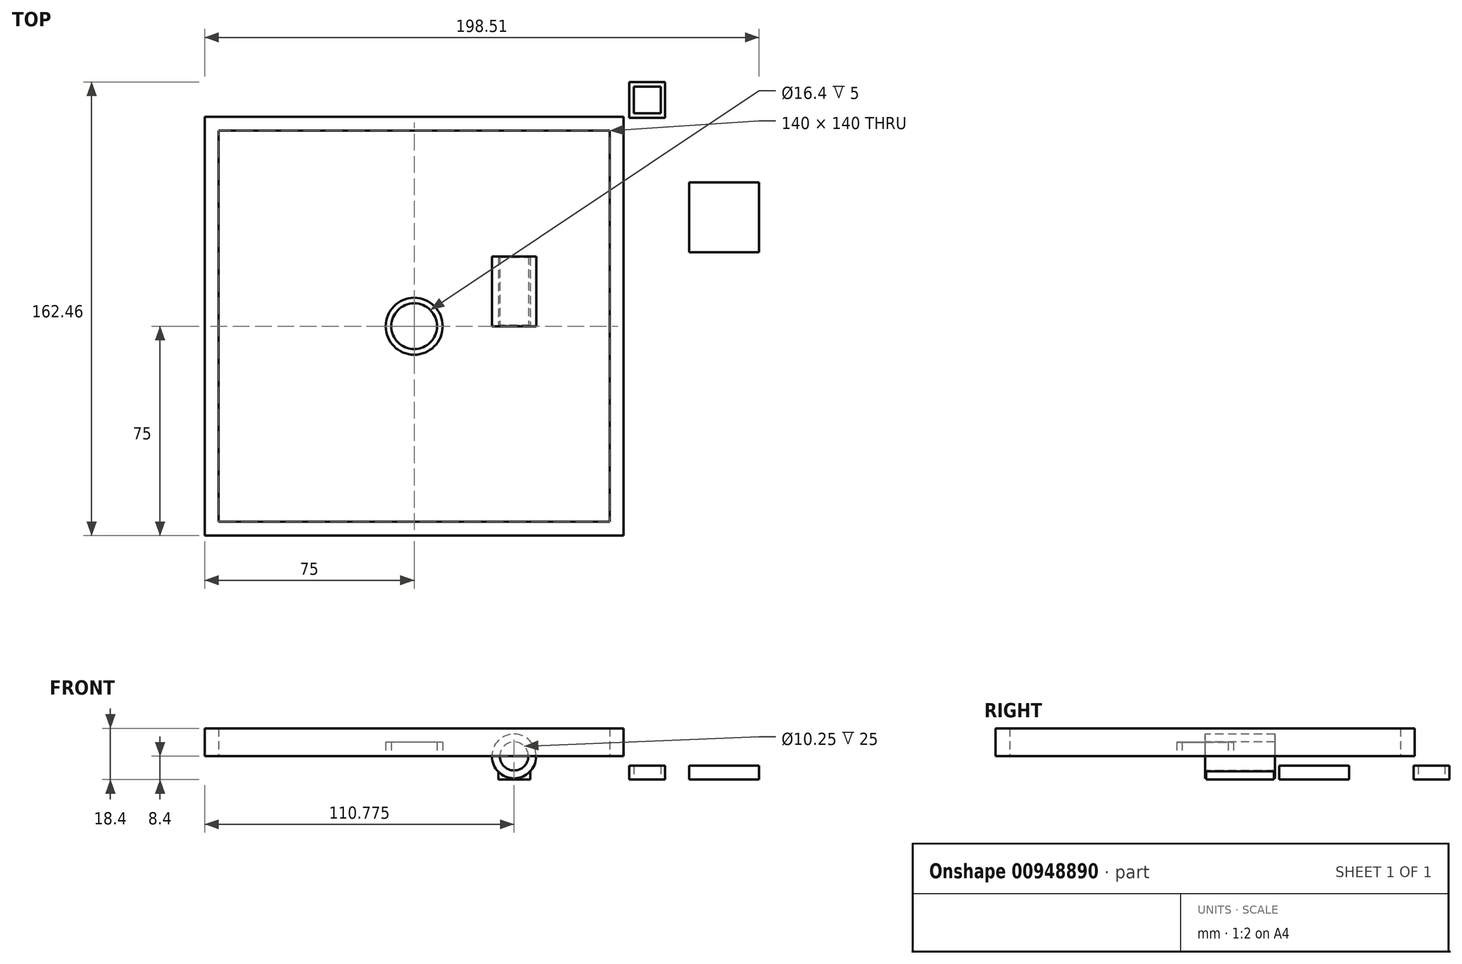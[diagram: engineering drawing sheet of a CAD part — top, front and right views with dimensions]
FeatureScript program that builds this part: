
annotation { "Feature Type Name" : "Feature", "Feature Type Description" : "" }
export const myFeature = defineFeature(function(context is Context, id is Id, definition is map)
    precondition{}
    {
        {
            var Q0;
            Q0=qCreatedBy(makeId("Top.planeOp"),FACE);
            var sketch = newSketch(context, id + "F0", { "sketchPlane" : qUnion([Q0])});
            skLineSegment(sketch, "E0.bottom", {"start": v(75, -75) * mm, "end": v(-75, -75) * mm});
            skLineSegment(sketch, "E0.top", {"start": v(75, 75) * mm, "end": v(-75, 75) * mm});
            skLineSegment(sketch, "E0.left", {"start": v(75, -75) * mm, "end": v(75, 75) * mm});
            skLineSegment(sketch, "E0.right", {"start": v(-75, -75) * mm, "end": v(-75, 75) * mm});
            skPoint(sketch, "E0.middle", {"position": v(0, 0) * mm});
            skLineSegment(sketch, "E1.bottom", {"start": v(70, -70) * mm, "end": v(-70, -70) * mm});
            skLineSegment(sketch, "E1.top", {"start": v(70, 70) * mm, "end": v(-70, 70) * mm});
            skLineSegment(sketch, "E1.left", {"start": v(70, -70) * mm, "end": v(70, 70) * mm});
            skLineSegment(sketch, "E1.right", {"start": v(-70, -70) * mm, "end": v(-70, 70) * mm});
            skCircle(sketch, "E2", {"center": v(0, 0) * mm, "radius": 8.2 * mm});
            skCircle(sketch, "E3", {"center": v(0, 0) * mm, "radius": 10.2 * mm});
            skCircle(sketch, "E4", {"center": v(35.77, 0) * mm, "radius": 5.12 * mm});
            skCircle(sketch, "E5", {"center": v(35.77, 0) * mm, "radius": 7.92 * mm});
            skLineSegment(sketch, "E6", {"start": v(0, 0) * mm, "end": v(-48.15, 0) * mm, "construction": true});
            skSolve(sketch);
        }
        {
            var Q0;
            Q0=makeQuery(id+"F0.imprint","IMPRINT",FACE,{"disambiguationData":[TD([[makeQuery(id+"F0.imprint","IMPRINT",EDGE,{"derivedFrom":sQuery(id+"F0.wireOp",EDGE,"E0.bottom")}),-1.0]])]});
            extrude(context, id + "F1", {"entities" : qUnion([Q0]), "depth" : 10 * mm, "offsetDistance" : 25 * mm});
        }
        {
            var Q0;
            Q0=makeQuery(id+"F0.imprint","IMPRINT",FACE,{"disambiguationData":[TD([[makeQuery(id+"F0.imprint","IMPRINT",EDGE,{"derivedFrom":sQuery(id+"F0.wireOp",EDGE,"E2")}),-1.0]])]});
            extrude(context, id + "F2", {"entities" : qUnion([Q0]), "depth" : 5 * mm, "offsetDistance" : 25 * mm});
        }
        {
            var Q0;
            Q0=makeQuery(id+"F0.imprint","IMPRINT",FACE,{"disambiguationData":[TD([[makeQuery(id+"F0.imprint","IMPRINT",EDGE,{"derivedFrom":sQuery(id+"F0.wireOp",EDGE,"E4")}),-1.0]])]});
            extrude(context, id + "F3", {"entities" : qUnion([Q0]), "depth" : 25 * mm, "offsetDistance" : 25 * mm});
        }
        {
            var Q0;
            Q0=makeQuery(id+"F3.opExtrude","SWEPT_BODY",BODY,{"disambiguationData":[OSD([sQuery(id+"F0.wireOp",EDGE,"E4"),sQuery(id+"F0.wireOp",EDGE,"E5")])]});
            var Q1;
            Q1=sQuery(id+"F0.wireOp",EDGE,"E6");
            var Q2;
            Q2=sQuery(id+"F0.wireOp",EDGE,"E6");
            transform(context, id + "F4", {"entities" : qUnion([Q0]), "transformType" : TransformType.ROTATION, "transformAxis" : qUnion([Q2]), "angle" : 90 * degree, "makeCopy" : false});
        }
        {
            var Q0;
            Q0=makeQuery(id+"F0.imprint","IMPRINT",FACE,{"disambiguationData":[TD([[makeQuery(id+"F0.imprint","IMPRINT",EDGE,{"derivedFrom":sQuery(id+"F0.wireOp",EDGE,"E1.bottom")}),-1.0]])]});
            cPlane(context, id + "F5", {"entities" : qUnion([Q0]), "cplaneType" : CPlaneType.OFFSET, "offset" : 8.4 * mm, "oppositeDirection" : true, "width" : 150 * mm, "height" : 150 * mm});
        }
        {
            var Q0;
            Q0=qCreatedBy(id+"F5.planeOp",FACE);
            var sketch = newSketch(context, id + "F6", { "sketchPlane" : qUnion([Q0])});
            skLineSegment(sketch, "E7.bottom", {"start": v(30.17, 24.7) * mm, "end": v(41.63, 24.7) * mm});
            skLineSegment(sketch, "E7.top", {"start": v(30.17, 0.33) * mm, "end": v(41.63, 0.33) * mm});
            skLineSegment(sketch, "E7.left", {"start": v(30.17, 24.7) * mm, "end": v(30.17, 0.33) * mm});
            skLineSegment(sketch, "E7.right", {"start": v(41.63, 24.7) * mm, "end": v(41.63, 0.33) * mm});
            skSolve(sketch);
        }
        {
            var Q0;
            Q0 = qSketchRegion(id + "F6", true);
            extrude(context, id + "F7", {"entities" : qUnion([Q0]), "operationType" : NewBodyOperationType.ADD, "depth" : 3 * mm, "offsetDistance" : 25 * mm});
        }
        {
            var Q0;
            Q0=qCreatedBy(id+"F5.planeOp",FACE);
            var sketch = newSketch(context, id + "F8", { "sketchPlane" : qUnion([Q0])});
            skLineSegment(sketch, "E8.bottom", {"start": v(89.87, 74.66) * mm, "end": v(77.07, 74.66) * mm});
            skLineSegment(sketch, "E8.top", {"start": v(89.87, 87.46) * mm, "end": v(77.07, 87.46) * mm});
            skLineSegment(sketch, "E8.left", {"start": v(89.87, 74.66) * mm, "end": v(89.87, 87.46) * mm});
            skLineSegment(sketch, "E8.right", {"start": v(77.07, 74.66) * mm, "end": v(77.07, 87.46) * mm});
            skPoint(sketch, "E8.middle", {"position": v(83.47, 81.06) * mm});
            skLineSegment(sketch, "E9.bottom", {"start": v(88.27, 85.86) * mm, "end": v(78.67, 85.86) * mm});
            skLineSegment(sketch, "E9.top", {"start": v(88.27, 76.26) * mm, "end": v(78.67, 76.26) * mm});
            skLineSegment(sketch, "E9.left", {"start": v(88.27, 85.86) * mm, "end": v(88.27, 76.26) * mm});
            skLineSegment(sketch, "E9.right", {"start": v(78.67, 85.86) * mm, "end": v(78.67, 76.26) * mm});
            skLineSegment(sketch, "E10.bottom", {"start": v(98.51, 51.53) * mm, "end": v(123.51, 51.53) * mm});
            skLineSegment(sketch, "E10.top", {"start": v(98.51, 26.53) * mm, "end": v(123.51, 26.53) * mm});
            skLineSegment(sketch, "E10.left", {"start": v(98.51, 51.53) * mm, "end": v(98.51, 26.53) * mm});
            skLineSegment(sketch, "E10.right", {"start": v(123.51, 51.53) * mm, "end": v(123.51, 26.53) * mm});
            skSolve(sketch);
        }
        {
            var Q0;
            Q0 = qSketchRegion(id + "F8", true);
            extrude(context, id + "F9", {"entities" : qUnion([Q0]), "depth" : 5 * mm, "offsetDistance" : 25 * mm});
        }
    });
